# Revit family: Genie_Site_ArticulatingBoom_(Z-45FE)a
name_source: partatom
category: Site
revit_build: Autodesk Revit 2018 (Build: 20190510_1515(x64)
units: mm (PartAtom-declared; Revit-internal decimal feet)

## family parameters
Always vertical = Yes
Cut with Voids When Loaded = No
OmniClass Number = 23.50.85.17.11
OmniClass Title = Electric and Battery Telescoping Platforms
Part Type = Normal
Round Connector Dimension = Use Diameter
Shared = No
Work Plane-Based = No

## types (1)
- Z-45FE
    Assembly Code = E1030900
    AssetType = Fixed
    BIMObjectName = Genie_Site_ArticulatingBoom_(Z-45FE)
    Black = Steel, Paint Finish, Black, Genie
    ClassificationName = Uniclass2015
    ClassificationValue = Pr_65_80_47_95
    Color = Grey & Blue
    Cost = 0 $
    Description = Two machines in one, the Genie® Z®-45 FE hybrid articulating boom lift is the ideal, environment-friendly solution for increased efficiency and low cost of operation. In ‘all-electric’ mode it offers a full work day of emissions-free run time on a single battery charge. In ‘hybrid’ mode, it offers one week of run time with a single tank of diesel.
    DocumentationLiterature = https://www.genielift.com
    DocumentationTechnical = https://www.genielift.com
    DurationUnit = Years
    ExpectedLife = 0
    Features = Two machines in one, the Genie® Z®-45 FE hybrid articulating boom lift is the ideal, environment-friendly solution for increased efficiency and low cost of operation. In ‘all-electric’ mode it offers a full work day of emissions-free run time on a single battery charge. In ‘hybrid’ mode, it offers one week of run time with a single tank of diesel.
    Finish = Painted Steel
    Grey = Steel, Paint Finish, Grey, Genie
    IfcExportAs = IfcTransportElement
    IfcExportType = IfcTransportElementType
    Keynote = X
    Manufacturer = Genie
    ManufacturerName = Genie
    Material = Painted Steel
    Model = Genie - Articulating Boom
    ModelNumber = Z-45FE
    ModelReference = Genie - Articulating Boom
    NBSDescription = Vertical lifting platforms
    NBSObjectName = Genie - Vertical lifting platforms
    NBSReference = 90-80-65/350
    NominalDepth = 2290 mm  [stored 7.51312 ft]
    NominalHeight = 2290 mm  [stored 7.51312 ft]
    NominalLength = 5870 mm  [stored 19.2585 ft]
    ProductionYear = 2020
    ReplacementCost = 0
    Size = 5.87m x 2.29m x 2.29m
    Tire = Rubber, Tire, Black
    Type Comments = Z-45FE
    TypeName = Genie - Articulating Boom
    URL = http://www.genielift.co.uk
    WarrantyDurationLabor = 0
    WarrantyDurationParts = 0
    WarrantyDurationUnit = Years
    WarrantyGuarantorLabor = http://www.genielift.co.uk
    WarrantyGuarantorParts = http://www.genielift.co.uk
    _BSBibleVersion = 16
    _BimSpecGuid = 0
    _CurrentRevision = 1
    _DistributedBy = www.bimstore.co.uk

note: [stored X ft] marks values corroborated as IEEE doubles in the binary element streams (Revit-internal decimal feet)

## geometry (parser evidence)
native form markers: Sweep x47
no freeform markers — native parametric forms only
